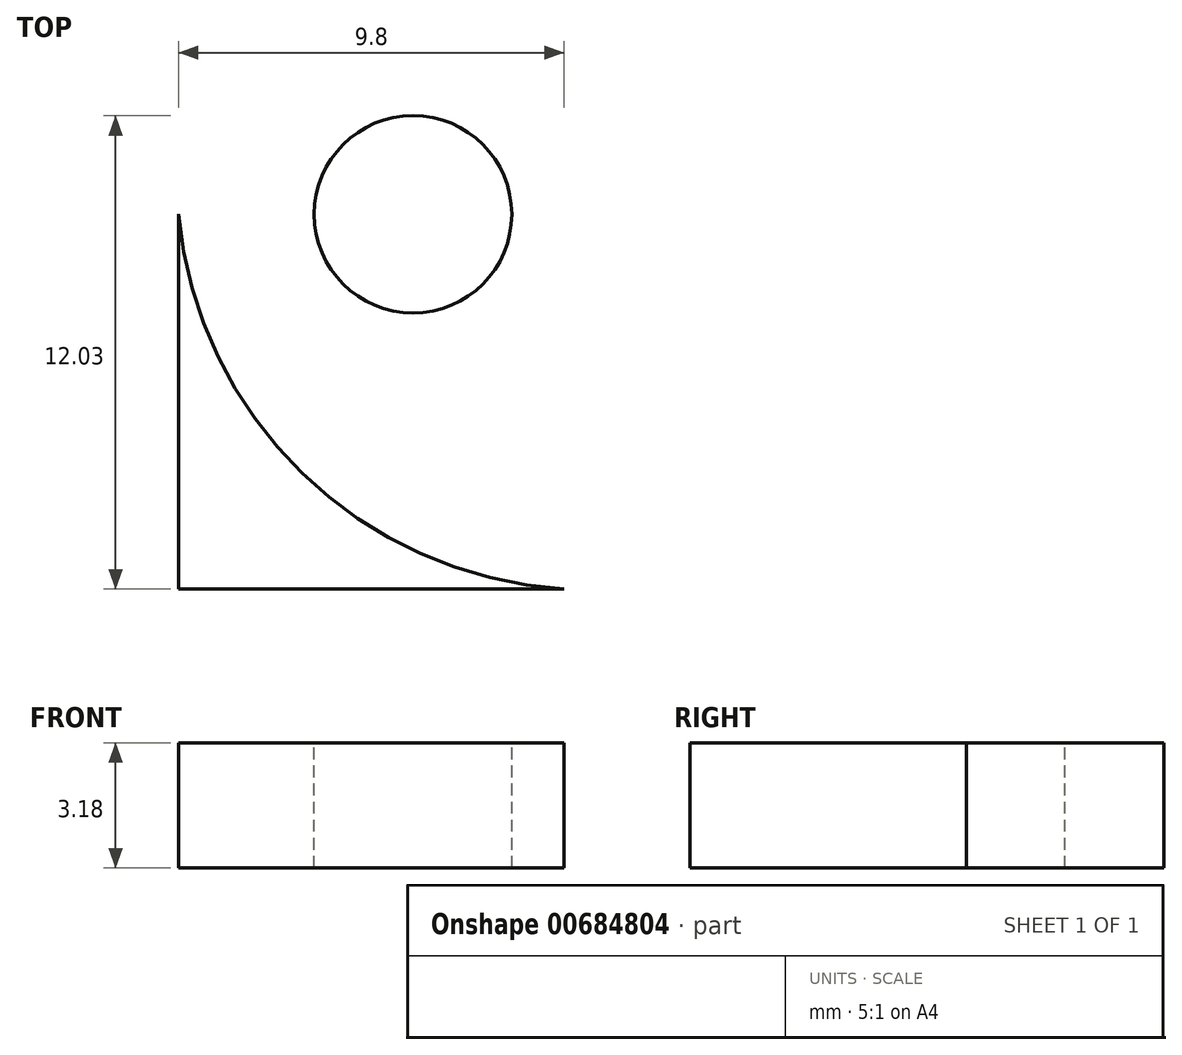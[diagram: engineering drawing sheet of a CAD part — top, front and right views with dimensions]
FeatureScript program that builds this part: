
annotation { "Feature Type Name" : "Feature", "Feature Type Description" : "" }
export const myFeature = defineFeature(function(context is Context, id is Id, definition is map)
    precondition{}
    {
        {
            var Q0;
            Q0=qCreatedBy(makeId("Top.planeOp"),FACE);
            var sketch = newSketch(context, id + "F0", { "sketchPlane" : qUnion([Q0])});
            skLineSegment(sketch, "E0.bottom", {"start": v(0, 0) * mm, "end": v(-38.1, 0) * mm});
            skLineSegment(sketch, "E0.top", {"start": v(0, 19.05) * mm, "end": v(-38.1, 19.05) * mm});
            skLineSegment(sketch, "E0.left", {"start": v(0, 0) * mm, "end": v(0, 19.05) * mm});
            skLineSegment(sketch, "E0.right", {"start": v(-38.1, 0) * mm, "end": v(-38.1, 19.05) * mm});
            skSolve(sketch);
        }
        {
            var Q0;
            Q0 = qSketchRegion(id + "F0", true);
            extrude(context, id + "F1", {"entities" : qUnion([Q0]), "depth" : 3.17 * mm, "offsetDistance" : 25.4 * mm});
        }
        {
            var Q0;
            Q0=makeQuery(id+"F1.opExtrude","CAP_FACE",FACE,{"disambiguationData":[OSD([sQuery(id+"F0.wireOp",EDGE,"E0.bottom"),sQuery(id+"F0.wireOp",EDGE,"E0.top"),sQuery(id+"F0.wireOp",EDGE,"E0.left"),sQuery(id+"F0.wireOp",EDGE,"E0.right")])],"isStart":false});
            var sketch = newSketch(context, id + "F2", { "sketchPlane" : qUnion([Q0])});
            skLineSegment(sketch, "E1", {"start": v(-38.1, 9.52) * mm, "end": v(0, 9.53) * mm});
            skArc(sketch, "E2", {"start": v(-28.3, 19.05) * mm, "mid": v(-34.96, 16.1) * mm, "end": v(-38.1, 9.52) * mm});
            skArc(sketch, "E3.MirrorCS", {"start": v(-28.3, 0) * mm, "mid": v(-34.96, 2.95) * mm, "end": v(-38.1, 9.52) * mm});
            skCircle(sketch, "E4", {"center": v(-32.14, 9.52) * mm, "radius": 2.5 * mm});
            skSolve(sketch);
        }
        {
            var Q0;
            {var subQ0=sQuery(id+"F2.wireOp",EDGE,"E2");Q0=makeQuery(id+"F2.imprint","IMPRINT",FACE,{"disambiguationData":[TD([[makeQuery(id+"F2.imprint","IMPRINT",EDGE,{"derivedFrom":subQ0}),-1.0]])]});}
            var Q1;
            {var subQ0=sQuery(id+"F2.wireOp",EDGE,"E3.MirrorCS");Q1=makeQuery(id+"F2.imprint","IMPRINT",FACE,{"disambiguationData":[TD([[makeQuery(id+"F2.imprint","IMPRINT",EDGE,{"derivedFrom":subQ0}),1.0]])]});}
            var Q2;
            {var subQ0=sQuery(id+"F2.wireOp",EDGE,"E4");var subQ1=sQuery(id+"F2.wireOp",EDGE,"E1");var subQ2=makeQuery(id+"F2.imprint","INTERSECT",VERTEX,{"disambiguationData":[OD(0.0)],"derivedFrom":[subQ1,subQ0]});Q2=makeQuery(id+"F2.imprint","IMPRINT",FACE,{"disambiguationData":[TD([[makeQuery(id+"F2.imprint","IMPRINT",EDGE,{"disambiguationData":[TD([[subQ2,-1.0]])],"derivedFrom":subQ1}),1.0]])]});}
            var Q3;
            {var subQ0=sQuery(id+"F2.wireOp",EDGE,"E4");var subQ1=sQuery(id+"F2.wireOp",EDGE,"E1");var subQ2=makeQuery(id+"F2.imprint","INTERSECT",VERTEX,{"disambiguationData":[OD(0.0)],"derivedFrom":[subQ1,subQ0]});Q3=makeQuery(id+"F2.imprint","IMPRINT",FACE,{"disambiguationData":[TD([[makeQuery(id+"F2.imprint","IMPRINT",EDGE,{"disambiguationData":[TD([[subQ2,-1.0]])],"derivedFrom":subQ1}),-1.0]])]});}
            extrude(context, id + "F3", {"entities" : qUnion([Q0, Q1, Q2, Q3]), "operationType" : NewBodyOperationType.REMOVE, "endBound" : BoundingType.THROUGH_ALL, "oppositeDirection" : true, "depth" : 25.4 * mm, "offsetDistance" : 25.4 * mm});
        }
    });
